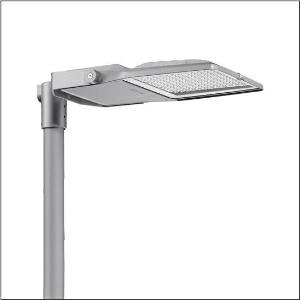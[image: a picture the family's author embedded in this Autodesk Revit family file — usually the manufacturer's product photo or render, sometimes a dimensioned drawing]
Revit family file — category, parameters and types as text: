
# Revit family: floodlight_fl_21_iq_midi___pl43_5xa7782f2a3a_db1b
name_source: partatom
category: Lighting Fixtures
units: mm (PartAtom-declared; Revit-internal decimal feet)

## family parameters
Cut with Voids When Loaded = No
Host = Face
Light Source = No
Part Type = Normal
Room Calculation Point = No
Round Connector Dimension = Use Diameter
Shared = No

## types (1)
- --- (1 x LED, 36680 lm, 270.2 W, 3000K)
    Apparent Load = 270 VA
    CIE Flux Codes = 27 78 99 100 100
    Color Rendering = 70
    Color Temperature = 3000K
    Default Elevation = 1800 mm
    Description = Floodlight FL 21 iQ midi, floodlight, primary light control with lens, of PMMA, primary optical cover: protective disc, of toughened safety glass, transparent, light distribution: PL43, light emission: direct distribution, installation type: surface-mounted, LED, High Power LED, rated luminous flux: 36.680lm, luminous efficacy: 136lm/W, light colour: 730, colour temperature: 3000K, control gear: ECG iQ, control: optimised constant luminous flux control (CLO 2.0), Desk-Remote (wireless, voltage-free reading and setting of iQ features in the workshop via application-optimized NFC function/RFID function), Smart-Wire, Night-Set, Temp-Guard, Auto-Match, Street-Remote, with terminal, 6-pole, mains connection: 220..240V, AC, 50/60Hz, start of lifetime: 270W, end of service life: 287W, reduction: 117W, luminaire housing, of diecast aluminium, powder-coated, Siteco® metallic grey (DB 702S), corrosivity category C5 mid according to DIN EN ISO 12944, sealing non-destructively replaceable, please order mast flange separately, mast bracket, of steel, galvanised, powder-coated, Siteco® metallic grey (DB 702S), protection rating (complete): IP66, insulation class (complete): insulation class II (safety insulation), certification: CE, protection symbol: D, impact resistance: IK08, permissible operating ambient temperature: -40..+40°C, permissible operating ambient temperature for outdoor applications: -40..+50°C, standard: DIN EN 12944, LABS conformity tested according to VDMA 24364:2018-05, packaging unit: 1 piece

Light Distribution: PL43
    Height = 76 mm
    Lamp = 1 x LED
    Lamp Light Flux = 36680 lm
    Lamp Power = 270.2 W
    Lamp count = 1
    Length = 657 mm
    Luminous efficacy = 136 lm/W
    Manufacturer = Siteco
    ModVariant = No
    Model = 5XA7782F2A3A
    Number of Poles = 1
    OnlyDefault = Yes
    Power Factor = 1
    Product Name = Floodlight FL 21 iQ midi | PL43
    Product group = floodlight | pylon annexe
    ProductGroupID = 6200
    Protection Class = Protection class II
    Protection Degree = IP 66
    RLX_Detail_Level = 1
    RLX_Emergency_Light_Flux = 0 lm
    RLX_Emergency_Type = 0
    RLX_Emergency_Type_DB = No
    RlxData = <blob elided: 153593 chars, md5=896e5b8a>
    Socket = socket
    Standby Power = 0 W
    System Light Flux = 36680 lm
    System Power = 270 W
    Type Comments = factory setting: luminous flux: 100 % | dim-lin: 254 | 620 mA
    Type Image = l_1007123.jpg
    URL = http://relux.com
    VarID = @adj_034825
    Voltage = 0 V
    Weight = 0.00 kg
    Width = 442 mm

## geometry (parser evidence)
native form markers: Blend x4, Sweep x13
no freeform markers — native parametric forms only
